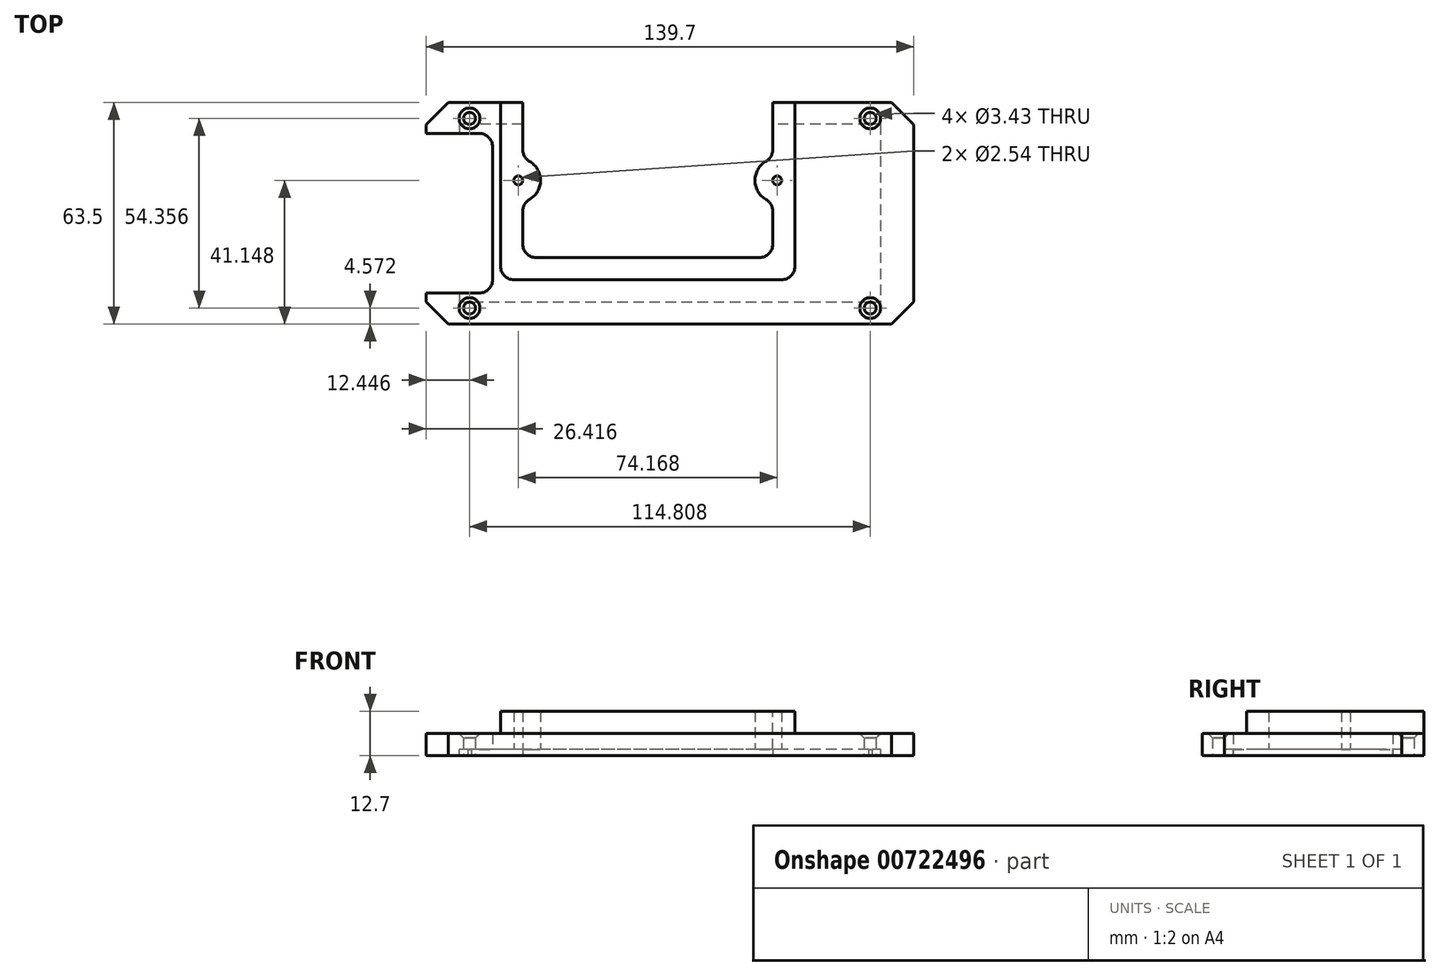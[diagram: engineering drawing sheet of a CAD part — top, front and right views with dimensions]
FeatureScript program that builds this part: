
annotation { "Feature Type Name" : "Feature", "Feature Type Description" : "" }
export const myFeature = defineFeature(function(context is Context, id is Id, definition is map)
    precondition{}
    {
        {
            var Q0;
            Q0=qCreatedBy(makeId("Top.planeOp"),FACE);
            var sketch = newSketch(context, id + "F0", { "sketchPlane" : qUnion([Q0])});
            skLineSegment(sketch, "E0.bottom", {"start": v(57.4, 27.18) * mm, "end": v(-57.4, 27.18) * mm, "construction": true});
            skLineSegment(sketch, "E0.top", {"start": v(57.4, -27.18) * mm, "end": v(-57.4, -27.18) * mm, "construction": true});
            skLineSegment(sketch, "E0.left", {"start": v(57.4, 27.18) * mm, "end": v(57.4, -27.18) * mm, "construction": true});
            skLineSegment(sketch, "E0.right", {"start": v(-57.4, 27.18) * mm, "end": v(-57.4, -27.18) * mm, "construction": true});
            skPoint(sketch, "E0.middle", {"position": v(0, 0) * mm});
            skLineSegment(sketch, "E1.bottom", {"start": v(69.85, 31.75) * mm, "end": v(29.46, 31.75) * mm});
            skLineSegment(sketch, "E1.top", {"start": v(69.85, -31.75) * mm, "end": v(-69.85, -31.75) * mm});
            skLineSegment(sketch, "E1.left", {"start": v(69.85, 31.75) * mm, "end": v(69.85, -31.75) * mm});
            skLineSegment(sketch, "E1.right", {"start": v(-69.85, 31.75) * mm, "end": v(-69.85, 22.86) * mm});
            skCircle(sketch, "E2", {"center": v(-57.4, 27.18) * mm, "radius": 1.71 * mm});
            skCircle(sketch, "E3", {"center": v(-57.4, -27.18) * mm, "radius": 1.71 * mm});
            skCircle(sketch, "E4", {"center": v(57.4, -27.18) * mm, "radius": 1.71 * mm});
            skCircle(sketch, "E5", {"center": v(57.4, 27.18) * mm, "radius": 1.71 * mm});
            skPoint(sketch, "E6.middle", {"position": v(0, 25.53) * mm});
            skLineSegment(sketch, "E7.0", {"start": v(30.73, 27.18) * mm, "end": v(30.73, -27.18) * mm, "construction": true});
            skLineSegment(sketch, "E8.0", {"start": v(-43.43, 27.18) * mm, "end": v(-43.43, -27.18) * mm, "construction": true});
            skLineSegment(sketch, "E9.0", {"start": v(57.4, 9.4) * mm, "end": v(-57.4, 9.4) * mm, "construction": true});
            skCircle(sketch, "E10", {"center": v(-43.43, 9.4) * mm, "radius": 1.27 * mm});
            skCircle(sketch, "E11", {"center": v(30.73, 9.4) * mm, "radius": 1.27 * mm});
            skLineSegment(sketch, "E12.trimOffspring", {"start": v(-42.16, 31.75) * mm, "end": v(-69.85, 31.75) * mm});
            skLineSegment(sketch, "E13.0", {"start": v(-50.8, 22.86) * mm, "end": v(-69.85, 22.86) * mm});
            skLineSegment(sketch, "E14.trimOffspring", {"start": v(-50.8, 22.86) * mm, "end": v(-50.8, -22.86) * mm});
            skLineSegment(sketch, "E15.trimOffspring", {"start": v(-50.8, -22.86) * mm, "end": v(-69.85, -22.86) * mm});
            skLineSegment(sketch, "E16.trimOffspring", {"start": v(-69.85, -22.86) * mm, "end": v(-69.85, -31.75) * mm});
            skLineSegment(sketch, "E17", {"start": v(29.46, 31.75) * mm, "end": v(29.46, 15.62) * mm});
            skLineSegment(sketch, "E18.trimOffspring", {"start": v(29.46, -12.7) * mm, "end": v(-42.16, -12.7) * mm});
            skLineSegment(sketch, "E19.trimOffspring", {"start": v(29.46, 3.18) * mm, "end": v(29.46, -12.7) * mm});
            skArc(sketch, "E20", {"start": v(29.46, 15.62) * mm, "mid": v(24.38, 9.4) * mm, "end": v(29.46, 3.18) * mm});
            skLineSegment(sketch, "E21", {"start": v(-42.16, 31.75) * mm, "end": v(-42.16, 15.62) * mm});
            skArc(sketch, "E22", {"start": v(-42.16, 3.18) * mm, "mid": v(-37.08, 9.4) * mm, "end": v(-42.16, 15.62) * mm});
            skLineSegment(sketch, "E23.trimOffspring", {"start": v(-42.16, 3.18) * mm, "end": v(-42.16, -12.7) * mm});
            skSolve(sketch);
        }
        {
            var Q0;
            Q0 = qSketchRegion(id + "F0", true);
            extrude(context, id + "F1", {"entities" : qUnion([Q0]), "depth" : 6.35 * mm, "offsetDistance" : 25.4 * mm});
        }
        {
            var Q0;
            Q0=qCreatedBy(makeId("Top.planeOp"),FACE);
            var sketch = newSketch(context, id + "F2", { "sketchPlane" : qUnion([Q0])});
            skLineSegment(sketch, "E24.bottom", {"start": v(60.32, 25.53) * mm, "end": v(-60.33, 25.53) * mm});
            skLineSegment(sketch, "E24.top", {"start": v(60.32, -25.53) * mm, "end": v(-60.33, -25.53) * mm});
            skLineSegment(sketch, "E24.left", {"start": v(60.32, 25.53) * mm, "end": v(60.32, -25.53) * mm});
            skLineSegment(sketch, "E24.right", {"start": v(-60.33, 25.53) * mm, "end": v(-60.33, -25.53) * mm});
            skSolve(sketch);
        }
        {
            var Q0;
            Q0 = qSketchRegion(id + "F2", true);
            extrude(context, id + "F3", {"entities" : qUnion([Q0]), "operationType" : NewBodyOperationType.REMOVE, "depth" : 1.78 * mm, "offsetDistance" : 25.4 * mm});
        }
        {
            var Q0;
            Q0=makeQuery(id+"F1.opExtrude","CAP_FACE",FACE,{"disambiguationData":[OSD([sQuery(id+"F0.wireOp",EDGE,"E1.bottom"),sQuery(id+"F0.wireOp",EDGE,"E1.top"),sQuery(id+"F0.wireOp",EDGE,"E1.left"),sQuery(id+"F0.wireOp",EDGE,"E1.right"),sQuery(id+"F0.wireOp",EDGE,"E2"),sQuery(id+"F0.wireOp",EDGE,"E3"),sQuery(id+"F0.wireOp",EDGE,"E4"),sQuery(id+"F0.wireOp",EDGE,"E5"),sQuery(id+"F0.wireOp",EDGE,"E10"),sQuery(id+"F0.wireOp",EDGE,"E11"),sQuery(id+"F0.wireOp",EDGE,"E12.trimOffspring"),sQuery(id+"F0.wireOp",EDGE,"E13.0"),sQuery(id+"F0.wireOp",EDGE,"E14.trimOffspring"),sQuery(id+"F0.wireOp",EDGE,"E15.trimOffspring"),sQuery(id+"F0.wireOp",EDGE,"E16.trimOffspring"),sQuery(id+"F0.wireOp",EDGE,"E17"),sQuery(id+"F0.wireOp",EDGE,"E18.trimOffspring"),sQuery(id+"F0.wireOp",EDGE,"E19.trimOffspring"),sQuery(id+"F0.wireOp",EDGE,"E20"),sQuery(id+"F0.wireOp",EDGE,"E21"),sQuery(id+"F0.wireOp",EDGE,"E22"),sQuery(id+"F0.wireOp",EDGE,"E23.trimOffspring")])],"isStart":false});
            var sketch = newSketch(context, id + "F4", { "sketchPlane" : qUnion([Q0])});
            skLineSegment(sketch, "E25", {"start": v(-48.51, -19.05) * mm, "end": v(-48.51, 31.75) * mm});
            skLineSegment(sketch, "E26", {"start": v(35.81, -19.05) * mm, "end": v(35.81, 31.75) * mm});
            skLineSegment(sketch, "E27", {"start": v(-48.51, -19.05) * mm, "end": v(35.81, -19.05) * mm});
            skLineSegment(sketch, "E28", {"start": v(-48.51, 31.75) * mm, "end": v(-42.16, 31.75) * mm});
            skLineSegment(sketch, "E29", {"start": v(29.46, 31.75) * mm, "end": v(35.81, 31.75) * mm});
            skArc(sketch, "E30.0", {"start": v(-42.16, 3.18) * mm, "mid": v(-37.08, 9.4) * mm, "end": v(-42.16, 15.62) * mm});
            skLineSegment(sketch, "E31.0", {"start": v(-42.16, 3.18) * mm, "end": v(-42.16, -12.7) * mm});
            skArc(sketch, "E32.0", {"start": v(29.46, 15.62) * mm, "mid": v(24.38, 9.4) * mm, "end": v(29.46, 3.18) * mm});
            skLineSegment(sketch, "E33.0", {"start": v(29.46, 3.18) * mm, "end": v(29.46, -12.7) * mm});
            skLineSegment(sketch, "E34.0.0", {"start": v(-42.16, 15.62) * mm, "end": v(-42.16, 31.75) * mm});
            skLineSegment(sketch, "E34.0.1", {"start": v(-42.16, 31.75) * mm, "end": v(-69.85, 31.75) * mm});
            skLineSegment(sketch, "E34.0.2", {"start": v(-69.85, 31.75) * mm, "end": v(-69.85, 22.86) * mm});
            skLineSegment(sketch, "E34.0.3", {"start": v(-69.85, 22.86) * mm, "end": v(-50.8, 22.86) * mm});
            skLineSegment(sketch, "E34.0.4", {"start": v(-50.8, 22.86) * mm, "end": v(-50.8, -22.86) * mm});
            skLineSegment(sketch, "E34.0.5", {"start": v(-50.8, -22.86) * mm, "end": v(-69.85, -22.86) * mm});
            skLineSegment(sketch, "E34.0.6", {"start": v(-69.85, -22.86) * mm, "end": v(-69.85, -31.75) * mm});
            skLineSegment(sketch, "E34.0.7", {"start": v(-69.85, -31.75) * mm, "end": v(69.85, -31.75) * mm});
            skLineSegment(sketch, "E34.0.8", {"start": v(69.85, -31.75) * mm, "end": v(69.85, 31.75) * mm});
            skLineSegment(sketch, "E34.0.9", {"start": v(69.85, 31.75) * mm, "end": v(29.46, 31.75) * mm});
            skLineSegment(sketch, "E34.0.10", {"start": v(29.46, 31.75) * mm, "end": v(29.46, 15.62) * mm});
            skLineSegment(sketch, "E34.0.13", {"start": v(29.46, -12.7) * mm, "end": v(-42.16, -12.7) * mm});
            skLineSegment(sketch, "E34.0.14", {"start": v(-42.16, -12.7) * mm, "end": v(-42.16, 3.18) * mm});
            skCircle(sketch, "E35.0", {"center": v(30.73, 9.4) * mm, "radius": 1.27 * mm});
            skCircle(sketch, "E36.0", {"center": v(-43.43, 9.4) * mm, "radius": 1.27 * mm});
            skSolve(sketch);
        }
        {
            var Q0;
            {var subQ2=sQuery(id+"F4.wireOp",EDGE,"E25");Q0=makeQuery(id+"F4.imprint","IMPRINT",FACE,{"disambiguationData":[TD([[makeQuery(id+"F4.imprint","IMPRINT",EDGE,{"derivedFrom":subQ2}),-1.0]])]});}
            extrude(context, id + "F5", {"entities" : qUnion([Q0]), "operationType" : NewBodyOperationType.ADD, "depth" : 6.35 * mm, "offsetDistance" : 25.4 * mm});
        }
        {
            var Q0;
            Q0=makeQuery(id+"F1.opExtrude","SWEPT_EDGE",EDGE,{"disambiguationData":[OSD([sQuery(id+"F0.wireOp",EDGE,"E1.right"),sQuery(id+"F0.wireOp",EDGE,"E12.trimOffspring")])]});
            var Q1;
            Q1=makeQuery(id+"F1.opExtrude","SWEPT_EDGE",EDGE,{"disambiguationData":[OSD([sQuery(id+"F0.wireOp",EDGE,"E1.bottom"),sQuery(id+"F0.wireOp",EDGE,"E1.left")])]});
            var Q2;
            Q2=makeQuery(id+"F1.opExtrude","SWEPT_EDGE",EDGE,{"disambiguationData":[OSD([sQuery(id+"F0.wireOp",EDGE,"E1.top"),sQuery(id+"F0.wireOp",EDGE,"E1.left")])]});
            var Q3;
            Q3=makeQuery(id+"F1.opExtrude","SWEPT_EDGE",EDGE,{"disambiguationData":[OSD([sQuery(id+"F0.wireOp",EDGE,"E1.top"),sQuery(id+"F0.wireOp",EDGE,"E1.left")])]});
            var Q4;
            Q4=makeQuery(id+"F1.opExtrude","SWEPT_EDGE",EDGE,{"disambiguationData":[OSD([sQuery(id+"F0.wireOp",EDGE,"E1.top"),sQuery(id+"F0.wireOp",EDGE,"E16.trimOffspring")])]});
            var Q5;
            Q5=makeQuery(id+"F1.opExtrude","SWEPT_EDGE",EDGE,{"disambiguationData":[OSD([sQuery(id+"F0.wireOp",EDGE,"E1.right"),sQuery(id+"F0.wireOp",EDGE,"E12.trimOffspring")])]});
            chamfer(context, id + "F6", {"entities" : qUnion([Q0, Q1, Q2, Q3, Q4, Q5]), "width" : 6.35 * mm, "tangentPropagation" : true});
        }
        {
            var Q0;
            Q0=makeQuery(id+"F1.opExtrude","SWEPT_EDGE",EDGE,{"disambiguationData":[OSD([sQuery(id+"F0.wireOp",EDGE,"E13.0"),sQuery(id+"F0.wireOp",EDGE,"E14.trimOffspring")])]});
            var Q1;
            Q1=makeQuery(id+"F1.opExtrude","SWEPT_EDGE",EDGE,{"disambiguationData":[OSD([sQuery(id+"F0.wireOp",EDGE,"E14.trimOffspring"),sQuery(id+"F0.wireOp",EDGE,"E15.trimOffspring")])]});
            var Q2;
            Q2=makeQuery(id+"F1.opExtrude","SWEPT_EDGE",EDGE,{"disambiguationData":[OSD([sQuery(id+"F0.wireOp",EDGE,"8b84f8d3-4f5a-4bc2-9ac2-7abf58bd3f75.0"),sQuery(id+"F0.wireOp",EDGE,"2878a425-7f2b-4253-aaa2-f9b63e65eb33.trimOffspring")])]});
            var Q3;
            Q3=makeQuery(id+"F1.opExtrude","SWEPT_EDGE",EDGE,{"disambiguationData":[OSD([sQuery(id+"F0.wireOp",EDGE,"f4d64e19-9dc3-4a0e-a3e6-541c1ec87e9f.trimOffspring"),sQuery(id+"F0.wireOp",EDGE,"91a84cb3-a648-4b21-bfb4-e165cf26adac.trimOffspring")])]});
            var Q4;
            Q4=makeQuery(id+"F1.opExtrude","SWEPT_EDGE",EDGE,{"disambiguationData":[OSD([sQuery(id+"F0.wireOp",EDGE,"63009cea-ed94-425f-9dbe-f2643fb30595.trimOffspring"),sQuery(id+"F0.wireOp",EDGE,"91a84cb3-a648-4b21-bfb4-e165cf26adac.trimOffspring")])]});
            var Q5;
            Q5=makeQuery(id+"F1.opExtrude","SWEPT_EDGE",EDGE,{"disambiguationData":[OSD([sQuery(id+"F0.wireOp",EDGE,"f718ab52-570f-47a8-bc3f-3e6e355cc182.0"),sQuery(id+"F0.wireOp",EDGE,"91065b18-5f9e-4757-aecb-778b453d1a58.0")])]});
            var Q6;
            Q6=makeQuery(id+"F1.opExtrude","SWEPT_EDGE",EDGE,{"disambiguationData":[OSD([sQuery(id+"F0.wireOp",EDGE,"519de364-4714-4318-9577-2c5a1bb1d778.trimOffspring"),sQuery(id+"F0.wireOp",EDGE,"f4d64e19-9dc3-4a0e-a3e6-541c1ec87e9f.trimOffspring")])]});
            var Q7;
            Q7=makeQuery(id+"F1.opExtrude","SWEPT_EDGE",EDGE,{"disambiguationData":[OSD([sQuery(id+"F0.wireOp",EDGE,"74cb45de-ccce-4692-b9bd-d122c502ac47.0"),sQuery(id+"F0.wireOp",EDGE,"63009cea-ed94-425f-9dbe-f2643fb30595.trimOffspring")])]});
            var Q8;
            Q8=makeQuery(id+"F1.opExtrude","SWEPT_EDGE",EDGE,{"disambiguationData":[OSD([sQuery(id+"F0.wireOp",EDGE,"E18.trimOffspring"),sQuery(id+"F0.wireOp",EDGE,"E19.trimOffspring")])]});
            var Q9;
            Q9=makeQuery(id+"F1.opExtrude","SWEPT_EDGE",EDGE,{"disambiguationData":[OSD([sQuery(id+"F0.wireOp",EDGE,"E18.trimOffspring"),sQuery(id+"F0.wireOp",EDGE,"E23.trimOffspring")])]});
            var Q10;
            Q10=makeQuery(id+"F1.opExtrude","SWEPT_EDGE",EDGE,{"disambiguationData":[OSD([sQuery(id+"F0.wireOp",EDGE,"E19.trimOffspring"),sQuery(id+"F0.wireOp",EDGE,"E20")])]});
            var Q11;
            Q11=makeQuery(id+"F1.opExtrude","SWEPT_EDGE",EDGE,{"disambiguationData":[OSD([sQuery(id+"F0.wireOp",EDGE,"E17"),sQuery(id+"F0.wireOp",EDGE,"E20")])]});
            var Q12;
            Q12=makeQuery(id+"F1.opExtrude","SWEPT_EDGE",EDGE,{"disambiguationData":[OSD([sQuery(id+"F0.wireOp",EDGE,"E21"),sQuery(id+"F0.wireOp",EDGE,"E22")])]});
            var Q13;
            Q13=makeQuery(id+"F1.opExtrude","SWEPT_EDGE",EDGE,{"disambiguationData":[OSD([sQuery(id+"F0.wireOp",EDGE,"E22"),sQuery(id+"F0.wireOp",EDGE,"E23.trimOffspring")])]});
            var Q14;
            Q14=makeQuery(id+"F5.opExtrude","SWEPT_EDGE",EDGE,{"disambiguationData":[OSD([sQuery(id+"FyoDTpN0qHeqAUc_1.wireOp",EDGE,"VMLBlQu9-rb5L-hNX0-yyqP-wW5oWhvgAdmn"),sQuery(id+"FyoDTpN0qHeqAUc_1.wireOp",EDGE,"g8S7eoAe-cfTD-in2x-wtEY-104PDUtKqJ5t")])]});
            var Q15;
            Q15=makeQuery(id+"F5.opExtrude","SWEPT_EDGE",EDGE,{"disambiguationData":[OSD([sQuery(id+"FyoDTpN0qHeqAUc_1.wireOp",EDGE,"DH6yYeBw-ZZOA-tWkK-8hEj-yUvDuHkT6Ruo"),sQuery(id+"FyoDTpN0qHeqAUc_1.wireOp",EDGE,"g8S7eoAe-cfTD-in2x-wtEY-104PDUtKqJ5t")])]});
            var Q16;
            Q16=makeQuery(id+"F5.opExtrude","SWEPT_EDGE",EDGE,{"disambiguationData":[OSD([sQuery(id+"F4.wireOp",EDGE,"E25"),sQuery(id+"F4.wireOp",EDGE,"E27")])]});
            var Q17;
            Q17=makeQuery(id+"F5.opExtrude","SWEPT_EDGE",EDGE,{"disambiguationData":[OSD([sQuery(id+"F4.wireOp",EDGE,"E26"),sQuery(id+"F4.wireOp",EDGE,"E27")])]});
            fillet(context, id + "F7", {"entities" : qUnion([Q0, Q1, Q2, Q3, Q4, Q5, Q6, Q7, Q8, Q9, Q10, Q11, Q12, Q13, Q14, Q15, Q16, Q17]), "radius" : 3.8 * mm, "tangentPropagation" : true, "allowEdgeOverflow" : false});
        }
        {
            var Q0;
            Q0=makeQuery(id+"F1.opExtrude","CAP_EDGE",EDGE,{"disambiguationData":[OSD([sQuery(id+"F0.wireOp",EDGE,"E3")])],"isStart":false});
            var Q1;
            Q1=makeQuery(id+"F1.opExtrude","CAP_EDGE",EDGE,{"disambiguationData":[OSD([sQuery(id+"F0.wireOp",EDGE,"E2")])],"isStart":false});
            var Q2;
            Q2=makeQuery(id+"F1.opExtrude","CAP_EDGE",EDGE,{"disambiguationData":[OSD([sQuery(id+"F0.wireOp",EDGE,"E5")])],"isStart":false});
            var Q3;
            Q3=makeQuery(id+"F1.opExtrude","CAP_EDGE",EDGE,{"disambiguationData":[OSD([sQuery(id+"F0.wireOp",EDGE,"E4")])],"isStart":false});
            chamfer(context, id + "F8", {"entities" : qUnion([Q0, Q1, Q2, Q3]), "width" : 1.27 * mm, "tangentPropagation" : true});
        }
    });
